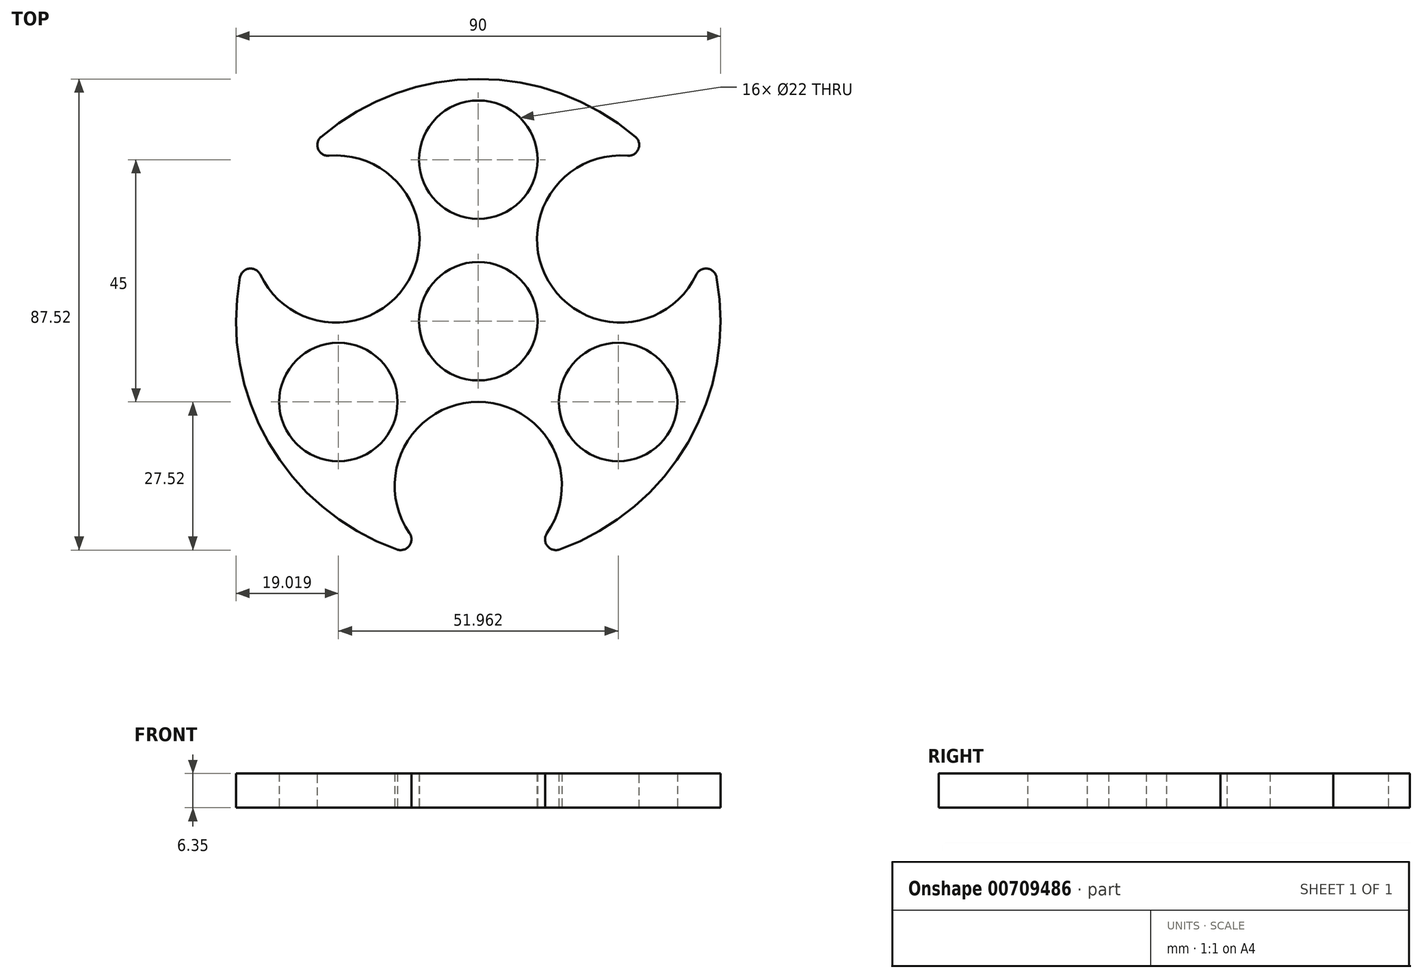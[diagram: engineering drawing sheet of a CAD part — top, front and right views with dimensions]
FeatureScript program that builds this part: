
annotation { "Feature Type Name" : "Feature", "Feature Type Description" : "" }
export const myFeature = defineFeature(function(context is Context, id is Id, definition is map)
    precondition{}
    {
        {
            var Q0;
            Q0=qCreatedBy(makeId("Top.planeOp"),FACE);
            var sketch = newSketch(context, id + "F0", { "sketchPlane" : qUnion([Q0])});
            skCircle(sketch, "E0", {"center": v(0, 0) * mm, "radius": 11 * mm});
            skCircle(sketch, "E1", {"center": v(-25.98, -15) * mm, "radius": 11 * mm});
            skCircle(sketch, "E2", {"center": v(25.98, -15) * mm, "radius": 11 * mm});
            skCircle(sketch, "E3", {"center": v(0, 30) * mm, "radius": 11 * mm});
            skArc(sketch, "E4", {"start": v(-41.93, 16.34) * mm, "mid": v(-38.97, -22.5) * mm, "end": v(-6.82, -44.48) * mm});
            skArc(sketch, "E5", {"start": v(-28.2, -0.16) * mm, "mid": v(-13, 7.5) * mm, "end": v(-13.96, 24.5) * mm});
            skArc(sketch, "E6", {"start": v(14.24, -24.34) * mm, "mid": v(0, -15) * mm, "end": v(-14.24, -24.34) * mm});
            skArc(sketch, "E7", {"start": v(6.82, -44.48) * mm, "mid": v(0, -15) * mm, "end": v(-6.82, -44.48) * mm});
            skArc(sketch, "E8", {"start": v(13.96, 24.5) * mm, "mid": v(13, 7.5) * mm, "end": v(28.2, -0.16) * mm});
            skArc(sketch, "E9", {"start": v(35.11, 28.14) * mm, "mid": v(13, 7.5) * mm, "end": v(41.93, 16.34) * mm});
            skArc(sketch, "E10", {"start": v(-41.93, 16.34) * mm, "mid": v(-13, 7.5) * mm, "end": v(-35.11, 28.14) * mm});
            skPoint(sketch, "E11.orphan", {"position": v(-29.53, 33.96) * mm});
            skArc(sketch, "E12.trimOffspring", {"start": v(6.82, -44.48) * mm, "mid": v(38.97, -22.5) * mm, "end": v(41.93, 16.34) * mm});
            skArc(sketch, "E13.trimOffspring", {"start": v(35.11, 28.14) * mm, "mid": v(0, 45) * mm, "end": v(-35.11, 28.14) * mm});
            skPoint(sketch, "E14.trimOffspring.end.orphan", {"position": v(29.53, 33.96) * mm});
            skSolve(sketch);
        }
        {
            var Q0;
            Q0=makeQuery(id+"F0.imprint","IMPRINT",FACE,{"disambiguationData":[TD([[makeQuery(id+"F0.imprint","IMPRINT",EDGE,{"derivedFrom":sQuery(id+"F0.wireOp",EDGE,"E0")}),-1.0]])]});
            extrude(context, id + "F1", {"entities" : qUnion([Q0]), "depth" : 6.35 * mm, "offsetDistance" : 25 * mm});
        }
        {
            var Q0;
            Q0=makeQuery(id+"F1.opExtrude","SWEPT_EDGE",EDGE,{"disambiguationData":[OSD([sQuery(id+"F0.wireOp",EDGE,"E7"),sQuery(id+"F0.wireOp",EDGE,"E12.trimOffspring")])]});
            var Q1;
            Q1=makeQuery(id+"F1.opExtrude","SWEPT_EDGE",EDGE,{"disambiguationData":[OSD([sQuery(id+"F0.wireOp",EDGE,"E4"),sQuery(id+"F0.wireOp",EDGE,"E7")])]});
            var Q2;
            Q2=makeQuery(id+"F1.opExtrude","SWEPT_EDGE",EDGE,{"disambiguationData":[OSD([sQuery(id+"F0.wireOp",EDGE,"E4"),sQuery(id+"F0.wireOp",EDGE,"E10")])]});
            var Q3;
            Q3=makeQuery(id+"F1.opExtrude","SWEPT_EDGE",EDGE,{"disambiguationData":[OSD([sQuery(id+"F0.wireOp",EDGE,"E10"),sQuery(id+"F0.wireOp",EDGE,"E13.trimOffspring")])]});
            var Q4;
            Q4=makeQuery(id+"F1.opExtrude","SWEPT_EDGE",EDGE,{"disambiguationData":[OSD([sQuery(id+"F0.wireOp",EDGE,"E9"),sQuery(id+"F0.wireOp",EDGE,"E13.trimOffspring")])]});
            var Q5;
            Q5=makeQuery(id+"F1.opExtrude","SWEPT_EDGE",EDGE,{"disambiguationData":[OSD([sQuery(id+"F0.wireOp",EDGE,"E9"),sQuery(id+"F0.wireOp",EDGE,"E12.trimOffspring")])]});
            fillet(context, id + "F2", {"entities" : qUnion([Q0, Q1, Q2, Q3, Q4, Q5]), "radius" : 2 * mm, "tangentPropagation" : true, "allowEdgeOverflow" : false});
        }
    });
